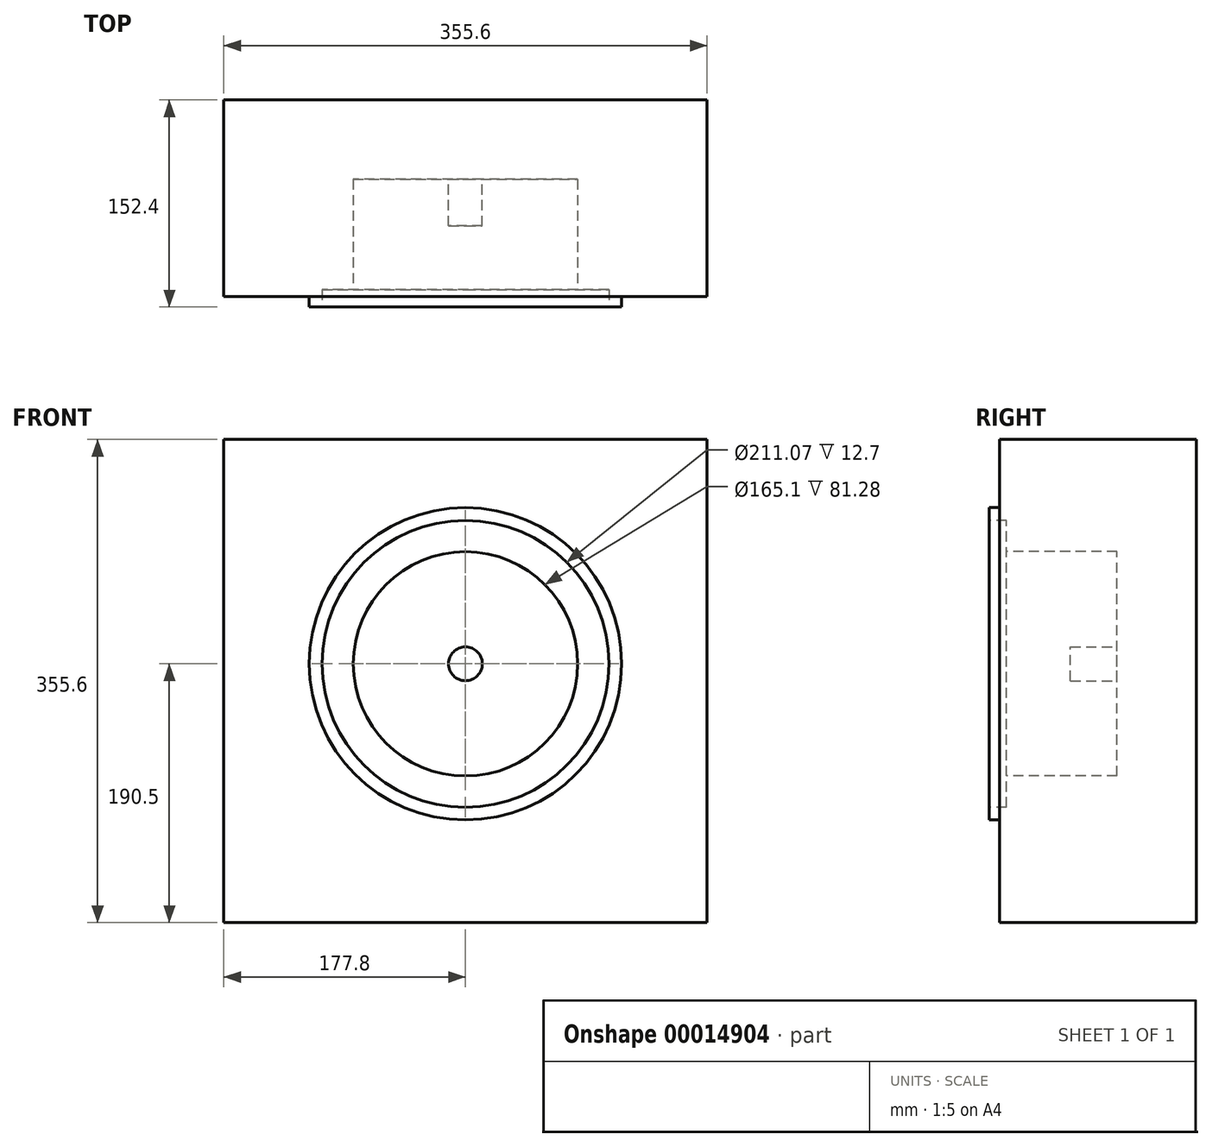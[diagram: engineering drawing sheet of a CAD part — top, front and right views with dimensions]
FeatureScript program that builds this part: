
annotation { "Feature Type Name" : "Feature", "Feature Type Description" : "" }
export const myFeature = defineFeature(function(context is Context, id is Id, definition is map)
    precondition{}
    {
        {
            var Q0;
            Q0=qCreatedBy(makeId("Front.planeOp"),FACE);
            var sketch = newSketch(context, id + "F0", { "sketchPlane" : qUnion([Q0])});
            skLineSegment(sketch, "E0.bottom", {"start": v(0, 0) * mm, "end": v(-355.6, 0) * mm});
            skLineSegment(sketch, "E0.top", {"start": v(0, 355.6) * mm, "end": v(-355.6, 355.6) * mm});
            skLineSegment(sketch, "E0.left", {"start": v(0, 0) * mm, "end": v(0, 355.6) * mm});
            skLineSegment(sketch, "E0.right", {"start": v(-355.6, 0) * mm, "end": v(-355.6, 355.6) * mm});
            skSolve(sketch);
        }
        {
            var Q0;
            Q0 = qSketchRegion(id + "F0", true);
            extrude(context, id + "F1", {"entities" : qUnion([Q0]), "depth" : 152.4 * mm});
        }
        {
            var Q0;
            Q0=makeQuery(id+"F1.opExtrude","CAP_FACE",FACE,{"disambiguationData":[OSD([sQuery(id+"F0.wireOp",EDGE,"E0.bottom"),sQuery(id+"F0.wireOp",EDGE,"E0.top"),sQuery(id+"F0.wireOp",EDGE,"E0.left"),sQuery(id+"F0.wireOp",EDGE,"E0.right")])],"isStart":false});
            var sketch = newSketch(context, id + "F2", { "sketchPlane" : qUnion([Q0])});
            skCircle(sketch, "E1", {"center": v(-177.8, 190.5) * mm, "radius": 114.94 * mm});
            skLineSegment(sketch, "E2.bottom", {"start": v(-355.6, 355.6) * mm, "end": v(0, 355.6) * mm});
            skLineSegment(sketch, "E2.top", {"start": v(-355.6, 0) * mm, "end": v(0, 0) * mm});
            skLineSegment(sketch, "E2.left", {"start": v(-355.6, 355.6) * mm, "end": v(-355.6, 0) * mm});
            skLineSegment(sketch, "E2.right", {"start": v(0, 355.6) * mm, "end": v(0, 0) * mm});
            skSolve(sketch);
        }
        {
            var Q0;
            Q0 = qSketchRegion(id + "F2", true);
            extrude(context, id + "F3", {"entities" : qUnion([Q0]), "operationType" : NewBodyOperationType.REMOVE, "oppositeDirection" : true, "depth" : 7.62 * mm});
        }
        {
            var Q0;
            Q0=makeQuery(id+"F1.opExtrude","CAP_FACE",FACE,{"disambiguationData":[OSD([sQuery(id+"F0.wireOp",EDGE,"E0.bottom"),sQuery(id+"F0.wireOp",EDGE,"E0.top"),sQuery(id+"F0.wireOp",EDGE,"E0.left"),sQuery(id+"F0.wireOp",EDGE,"E0.right")])],"isStart":false});
            var sketch = newSketch(context, id + "F4", { "sketchPlane" : qUnion([Q0])});
            skCircle(sketch, "E3", {"center": v(-177.8, 190.5) * mm, "radius": 105.54 * mm});
            skSolve(sketch);
        }
        {
            var Q0;
            Q0 = qSketchRegion(id + "F4", true);
            extrude(context, id + "F5", {"entities" : qUnion([Q0]), "operationType" : NewBodyOperationType.REMOVE, "oppositeDirection" : true, "depth" : 12.7 * mm});
        }
        {
            var Q0;
            Q0=makeQuery(id+"F1.opExtrude","CAP_FACE",FACE,{"disambiguationData":[OSD([sQuery(id+"F0.wireOp",EDGE,"E0.bottom"),sQuery(id+"F0.wireOp",EDGE,"E0.top"),sQuery(id+"F0.wireOp",EDGE,"E0.left"),sQuery(id+"F0.wireOp",EDGE,"E0.right")])],"isStart":false});
            var sketch = newSketch(context, id + "F6", { "sketchPlane" : qUnion([Q0])});
            skCircle(sketch, "E4", {"center": v(-177.8, 190.5) * mm, "radius": 82.55 * mm});
            skSolve(sketch);
        }
        {
            var Q0;
            Q0 = qSketchRegion(id + "F6", true);
            extrude(context, id + "F7", {"entities" : qUnion([Q0]), "operationType" : NewBodyOperationType.REMOVE, "oppositeDirection" : true, "depth" : 93.98 * mm});
        }
        {
            var Q0;
            Q0=makeQuery(id+"F7.boolean.opBoolean","COPY",FACE,{"derivedFrom":makeQuery(id+"F7.opExtrude","CAP_FACE",FACE,{"disambiguationData":[OSD([sQuery(id+"F6.wireOp",EDGE,"E4")])],"isStart":false})});
            var sketch = newSketch(context, id + "F8", { "sketchPlane" : qUnion([Q0])});
            skCircle(sketch, "E5", {"center": v(-177.8, 190.5) * mm, "radius": 12.43 * mm});
            skSolve(sketch);
        }
        {
            var Q0;
            Q0 = qSketchRegion(id + "F8", true);
            extrude(context, id + "F9", {"entities" : qUnion([Q0]), "operationType" : NewBodyOperationType.ADD, "depth" : 34.3 * mm});
        }
    });
